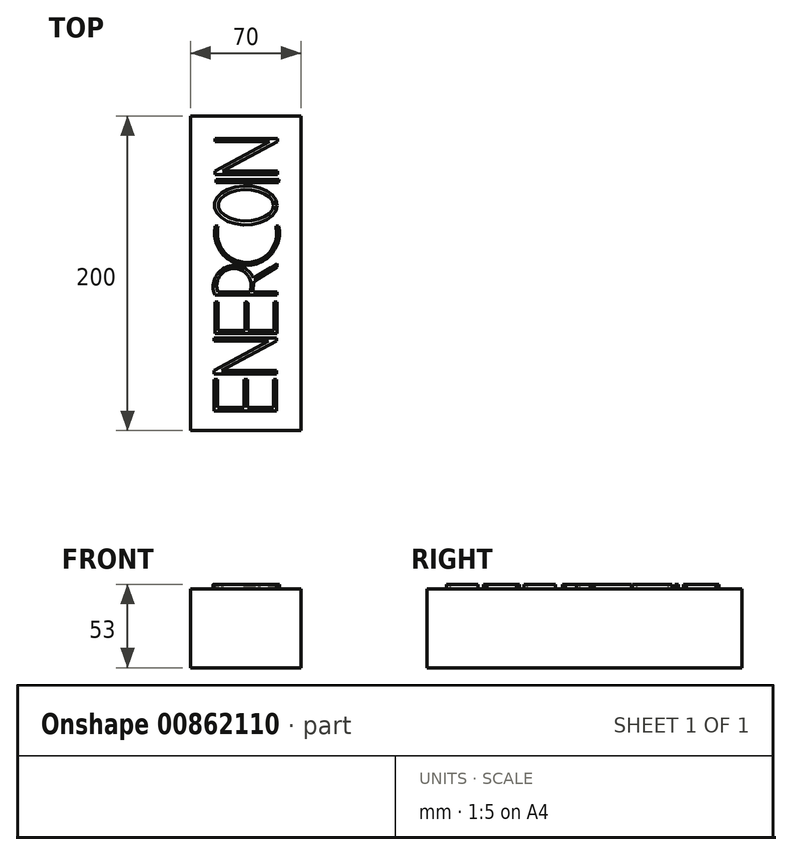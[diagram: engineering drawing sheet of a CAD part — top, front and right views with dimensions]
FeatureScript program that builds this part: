
annotation { "Feature Type Name" : "Feature", "Feature Type Description" : "" }
export const myFeature = defineFeature(function(context is Context, id is Id, definition is map)
    precondition{}
    {
        {
            var Q0;
            Q0=qCreatedBy(makeId("Front.planeOp"),FACE);
            var sketch = newSketch(context, id + "F0", { "sketchPlane" : qUnion([Q0])});
            skLineSegment(sketch, "E0.bottom", {"start": v(-35, 25) * mm, "end": v(35, 25) * mm});
            skLineSegment(sketch, "E0.top", {"start": v(-35, -25) * mm, "end": v(35, -25) * mm});
            skLineSegment(sketch, "E0.left", {"start": v(-35, 25) * mm, "end": v(-35, -25) * mm});
            skLineSegment(sketch, "E0.right", {"start": v(35, 25) * mm, "end": v(35, -25) * mm});
            skPoint(sketch, "E0.middle", {"position": v(0, 0) * mm});
            skSolve(sketch);
        }
        {
            var Q0;
            Q0=makeQuery(id+"F0.imprint","IMPRINT",FACE,{"disambiguationData":[TD([[makeQuery(id+"F0.imprint","IMPRINT",EDGE,{"derivedFrom":sQuery(id+"F0.wireOp",EDGE,"E0.bottom")}),-1.0]])]});
            extrude(context, id + "F1", {"entities" : qUnion([Q0]), "depth" : 130 * mm, "offsetDistance" : 25 * mm, "hasSecondDirection" : true, "secondDirectionOppositeDirection" : true, "secondDirectionDepth" : 70 * mm});
        }
        {
            var Q0;
            Q0=makeQuery(id+"F1.opExtrude","SWEPT_FACE",FACE,{"disambiguationData":[OSD([sQuery(id+"F0.wireOp",EDGE,"E0.bottom")])]});
            var sketch = newSketch(context, id + "F2", { "sketchPlane" : qUnion([Q0])});
            skLineSegment(sketch, "E1", {"start": v(0, -117.37) * mm, "end": v(-20, -117.37) * mm});
            skLineSegment(sketch, "E2", {"start": v(-20, -117.37) * mm, "end": v(-20, -97.37) * mm});
            skLineSegment(sketch, "E3", {"start": v(-20, -97.37) * mm, "end": v(-18, -97.37) * mm});
            skLineSegment(sketch, "E4", {"start": v(-18, -97.37) * mm, "end": v(-18, -115.37) * mm});
            skLineSegment(sketch, "E5", {"start": v(-18, -115.37) * mm, "end": v(-1, -115.37) * mm});
            skLineSegment(sketch, "E6", {"start": v(-1, -115.37) * mm, "end": v(-1, -97.37) * mm});
            skLineSegment(sketch, "E7", {"start": v(-1, -97.37) * mm, "end": v(1, -97.37) * mm});
            skLineSegment(sketch, "E8", {"start": v(1, -97.37) * mm, "end": v(1, -115.37) * mm});
            skLineSegment(sketch, "E9", {"start": v(1, -115.37) * mm, "end": v(17.49, -115.37) * mm});
            skLineSegment(sketch, "E10", {"start": v(17.49, -115.37) * mm, "end": v(17.49, -97.37) * mm});
            skLineSegment(sketch, "E11", {"start": v(17.49, -97.37) * mm, "end": v(19.49, -97.37) * mm});
            skLineSegment(sketch, "E12", {"start": v(19.49, -97.37) * mm, "end": v(19.49, -117.37) * mm});
            skLineSegment(sketch, "E13", {"start": v(19.49, -117.37) * mm, "end": v(0, -117.37) * mm});
            skLineSegment(sketch, "E14", {"start": v(-20, -93.87) * mm, "end": v(19.49, -93.87) * mm});
            skLineSegment(sketch, "E15", {"start": v(19.49, -93.87) * mm, "end": v(19.49, -91.87) * mm});
            skLineSegment(sketch, "E16", {"start": v(19.49, -91.87) * mm, "end": v(-15.32, -91.87) * mm});
            skLineSegment(sketch, "E17", {"start": v(-15.32, -91.87) * mm, "end": v(19.49, -73.17) * mm});
            skLineSegment(sketch, "E18", {"start": v(19.49, -73.17) * mm, "end": v(19.49, -71.17) * mm});
            skLineSegment(sketch, "E19", {"start": v(19.49, -71.17) * mm, "end": v(-20, -71.17) * mm});
            skLineSegment(sketch, "E20", {"start": v(-20, -71.17) * mm, "end": v(-20, -73.17) * mm});
            skLineSegment(sketch, "E21", {"start": v(-20, -73.17) * mm, "end": v(14.46, -73.17) * mm});
            skLineSegment(sketch, "E22", {"start": v(14.46, -73.17) * mm, "end": v(-20, -91.87) * mm});
            skLineSegment(sketch, "E23", {"start": v(-20, -91.87) * mm, "end": v(-20, -93.87) * mm});
            skLineSegment(sketch, "E24", {"start": v(0.43, -68.37) * mm, "end": v(-19.57, -68.37) * mm});
            skLineSegment(sketch, "E25", {"start": v(-19.57, -68.37) * mm, "end": v(-19.57, -48.37) * mm});
            skLineSegment(sketch, "E26", {"start": v(-19.57, -48.37) * mm, "end": v(-17.57, -48.37) * mm});
            skLineSegment(sketch, "E27", {"start": v(-17.57, -48.37) * mm, "end": v(-17.57, -66.37) * mm});
            skLineSegment(sketch, "E28", {"start": v(-17.57, -66.37) * mm, "end": v(-0.57, -66.37) * mm});
            skLineSegment(sketch, "E29", {"start": v(-0.57, -66.37) * mm, "end": v(-0.57, -48.37) * mm});
            skLineSegment(sketch, "E30", {"start": v(-0.57, -48.37) * mm, "end": v(1.43, -48.37) * mm});
            skLineSegment(sketch, "E31", {"start": v(1.43, -48.37) * mm, "end": v(1.43, -66.37) * mm});
            skLineSegment(sketch, "E32", {"start": v(1.43, -66.37) * mm, "end": v(17.91, -66.37) * mm});
            skLineSegment(sketch, "E33", {"start": v(17.91, -66.37) * mm, "end": v(17.91, -48.37) * mm});
            skLineSegment(sketch, "E34", {"start": v(17.91, -48.37) * mm, "end": v(19.91, -48.37) * mm});
            skLineSegment(sketch, "E35", {"start": v(19.91, -48.37) * mm, "end": v(19.91, -68.37) * mm});
            skLineSegment(sketch, "E36", {"start": v(19.91, -68.37) * mm, "end": v(0.43, -68.37) * mm});
            skLineSegment(sketch, "E37", {"start": v(19.91, -43.86) * mm, "end": v(-19.57, -43.86) * mm});
            skPoint(sketch, "E38.second.point", {"position": v(4.92, -28.04) * mm});
            skPoint(sketch, "E38.third.point", {"position": v(-7.93, -23.94) * mm});
            skArc(sketch, "E39", {"start": v(16.23, -26.25) * mm, "mid": v(16.2, -26.23) * mm, "end": v(16.17, -26.2) * mm});
            skPoint(sketch, "E39.second.point", {"position": v(1.43, -25.4) * mm});
            skPoint(sketch, "E39.third.point", {"position": v(11.21, -23.94) * mm});
            skLineSegment(sketch, "E40", {"start": v(19.91, -43.86) * mm, "end": v(19.91, -41.86) * mm});
            skLineSegment(sketch, "E41", {"start": v(19.91, -41.86) * mm, "end": v(4.92, -41.86) * mm});
            skArc(sketch, "E42", {"start": v(2.66, -41.86) * mm, "mid": v(-7.51, -26.92) * mm, "end": v(-17.68, -41.86) * mm});
            skPoint(sketch, "E42.first.point", {"position": v(-18.09, -40.62) * mm});
            skPoint(sketch, "E42.second.point", {"position": v(2.83, -34.3) * mm});
            skPoint(sketch, "E42.third.point", {"position": v(-8.15, -26.93) * mm});
            skArc(sketch, "E43", {"start": v(8.3, -43.67) * mm, "mid": v(8.5, -43.77) * mm, "end": v(8.7, -43.86) * mm});
            skPoint(sketch, "E43.second.point", {"position": v(21.7, -37.12) * mm});
            skPoint(sketch, "E43.third.point", {"position": v(16.23, -26.25) * mm});
            skLineSegment(sketch, "E44", {"start": v(4.92, -33.02) * mm, "end": v(19.91, -23.94) * mm});
            skArc(sketch, "E45.trimOffspring", {"start": v(8.22, -43.86) * mm, "mid": v(8.26, -43.76) * mm, "end": v(8.3, -43.67) * mm});
            skArc(sketch, "E46.trimOffspring", {"start": v(0.67, -48.37) * mm, "mid": v(1.05, -48.61) * mm, "end": v(1.43, -48.84) * mm});
            skPoint(sketch, "E47.orphan", {"position": v(-18.09, -41.86) * mm});
            skArc(sketch, "E48.trimOffspring", {"start": v(16.23, -26.25) * mm, "mid": v(16.2, -26.23) * mm, "end": v(16.16, -26.22) * mm});
            skArc(sketch, "E49", {"start": v(1.24, -48.73) * mm, "mid": v(1.34, -48.65) * mm, "end": v(1.43, -48.58) * mm});
            skPoint(sketch, "E49.second.point", {"position": v(4.92, -33.02) * mm});
            skPoint(sketch, "E49.third.point", {"position": v(4.92, -43.86) * mm});
            skArc(sketch, "E50.trimOffspring", {"start": v(4.92, -33.02) * mm, "mid": v(-12.74, -26.19) * mm, "end": v(-19.57, -43.86) * mm});
            skLineSegment(sketch, "E51", {"start": v(19.91, -23.94) * mm, "end": v(19.91, -25.94) * mm});
            skLineSegment(sketch, "E52", {"start": v(19.91, -25.94) * mm, "end": v(5.57, -34.87) * mm});
            skArc(sketch, "E53", {"start": v(5.57, -34.87) * mm, "mid": v(4.8, -38.32) * mm, "end": v(4.92, -41.86) * mm});
            skLineSegment(sketch, "E54.trimOffspring", {"start": v(2.66, -41.86) * mm, "end": v(-17.68, -41.86) * mm});
            skArc(sketch, "E55", {"start": v(-19.38, 0) * mm, "mid": v(0.78, -24.94) * mm, "end": v(20.94, 0) * mm});
            skPoint(sketch, "E55.first.point", {"position": v(19.91, -12) * mm});
            skPoint(sketch, "E55.third.point", {"position": v(-14.01, -18.68) * mm});
            skArc(sketch, "E56", {"start": v(-17.55, 0) * mm, "mid": v(0.78, -23.15) * mm, "end": v(19.11, 0) * mm});
            skLineSegment(sketch, "E57", {"start": v(-19.38, 0) * mm, "end": v(-17.55, 0) * mm});
            skLineSegment(sketch, "E58", {"start": v(19.11, 0) * mm, "end": v(20.94, 0) * mm});
            skEllipse(sketch, "E59", {"center": v(0, 13.16) * mm, "majorRadius": 19.95 * mm, "minorRadius": 12.42 * mm, "majorAxis": v(1, 0)});
            skEllipse(sketch, "E60", {"center": v(0, 13.16) * mm, "majorRadius": 17.5 * mm, "minorRadius": 9.93 * mm, "majorAxis": v(1, 0)});
            skLineSegment(sketch, "E61", {"start": v(20.94, 27.68) * mm, "end": v(21.02, 29.68) * mm});
            skLineSegment(sketch, "E62", {"start": v(21.02, 29.68) * mm, "end": v(-18.98, 29.68) * mm});
            skLineSegment(sketch, "E63", {"start": v(-18.98, 29.68) * mm, "end": v(-18.92, 27.68) * mm});
            skLineSegment(sketch, "E64", {"start": v(-18.92, 27.68) * mm, "end": v(20.94, 27.68) * mm});
            skLineSegment(sketch, "E65", {"start": v(-19.38, 32.86) * mm, "end": v(20.1, 32.86) * mm});
            skLineSegment(sketch, "E66", {"start": v(20.1, 32.86) * mm, "end": v(20.1, 34.86) * mm});
            skLineSegment(sketch, "E67", {"start": v(20.1, 34.86) * mm, "end": v(-14.7, 34.86) * mm});
            skLineSegment(sketch, "E68", {"start": v(-14.7, 34.86) * mm, "end": v(20.1, 53.56) * mm});
            skLineSegment(sketch, "E69", {"start": v(20.1, 53.56) * mm, "end": v(20.1, 55.56) * mm});
            skLineSegment(sketch, "E70", {"start": v(20.1, 55.56) * mm, "end": v(-19.38, 55.56) * mm});
            skLineSegment(sketch, "E71", {"start": v(-19.38, 55.56) * mm, "end": v(-19.38, 53.56) * mm});
            skLineSegment(sketch, "E72", {"start": v(-19.38, 53.56) * mm, "end": v(15.08, 53.56) * mm});
            skLineSegment(sketch, "E73", {"start": v(15.08, 53.56) * mm, "end": v(-19.38, 34.86) * mm});
            skLineSegment(sketch, "E74", {"start": v(-19.38, 34.86) * mm, "end": v(-19.38, 32.86) * mm});
            skSolve(sketch);
        }
        {
            var Q0;
            Q0=makeQuery(id+"F2.imprint","IMPRINT",FACE,{"disambiguationData":[TD([[makeQuery(id+"F2.imprint","IMPRINT",EDGE,{"derivedFrom":sQuery(id+"F2.wireOp",EDGE,"E1")}),-1.0]])]});
            var Q1;
            {var subQ1=sQuery(id+"F2.wireOp",EDGE,"E39");Q1=makeQuery(id+"F2.imprint","IMPRINT",FACE,{"disambiguationData":[TD([[makeQuery(id+"F2.imprint","IMPRINT",EDGE,{"derivedFrom":subQ1}),-1.0]])]});}
            var Q2;
            Q2=makeQuery(id+"F2.imprint","IMPRINT",FACE,{"disambiguationData":[TD([[makeQuery(id+"F2.imprint","IMPRINT",EDGE,{"derivedFrom":sQuery(id+"F2.wireOp",EDGE,"E55")}),1.0]])]});
            var Q3;
            Q3=makeQuery(id+"F2.imprint","IMPRINT",FACE,{"disambiguationData":[TD([[makeQuery(id+"F2.imprint","IMPRINT",EDGE,{"derivedFrom":sQuery(id+"F2.wireOp",EDGE,"E24")}),-1.0]])]});
            var Q4;
            Q4=makeQuery(id+"F2.imprint","IMPRINT",FACE,{"disambiguationData":[TD([[makeQuery(id+"F2.imprint","IMPRINT",EDGE,{"derivedFrom":sQuery(id+"F2.wireOp",EDGE,"E14")}),1.0]])]});
            var Q5;
            Q5=makeQuery(id+"F2.imprint","IMPRINT",FACE,{"disambiguationData":[TD([[makeQuery(id+"F2.imprint","IMPRINT",EDGE,{"derivedFrom":sQuery(id+"F2.wireOp",EDGE,"E59")}),1.0]])]});
            var Q6;
            Q6=makeQuery(id+"F2.imprint","IMPRINT",FACE,{"disambiguationData":[TD([[makeQuery(id+"F2.imprint","IMPRINT",EDGE,{"derivedFrom":sQuery(id+"F2.wireOp",EDGE,"E61")}),1.0]])]});
            var Q7;
            Q7=makeQuery(id+"F2.imprint","IMPRINT",FACE,{"disambiguationData":[TD([[makeQuery(id+"F2.imprint","IMPRINT",EDGE,{"derivedFrom":sQuery(id+"F2.wireOp",EDGE,"E65")}),1.0]])]});
            extrude(context, id + "F3", {"entities" : qUnion([Q0, Q1, Q2, Q3, Q4, Q5, Q6, Q7]), "operationType" : NewBodyOperationType.ADD, "depth" : 3 * mm, "offsetDistance" : 25 * mm});
        }
    });
